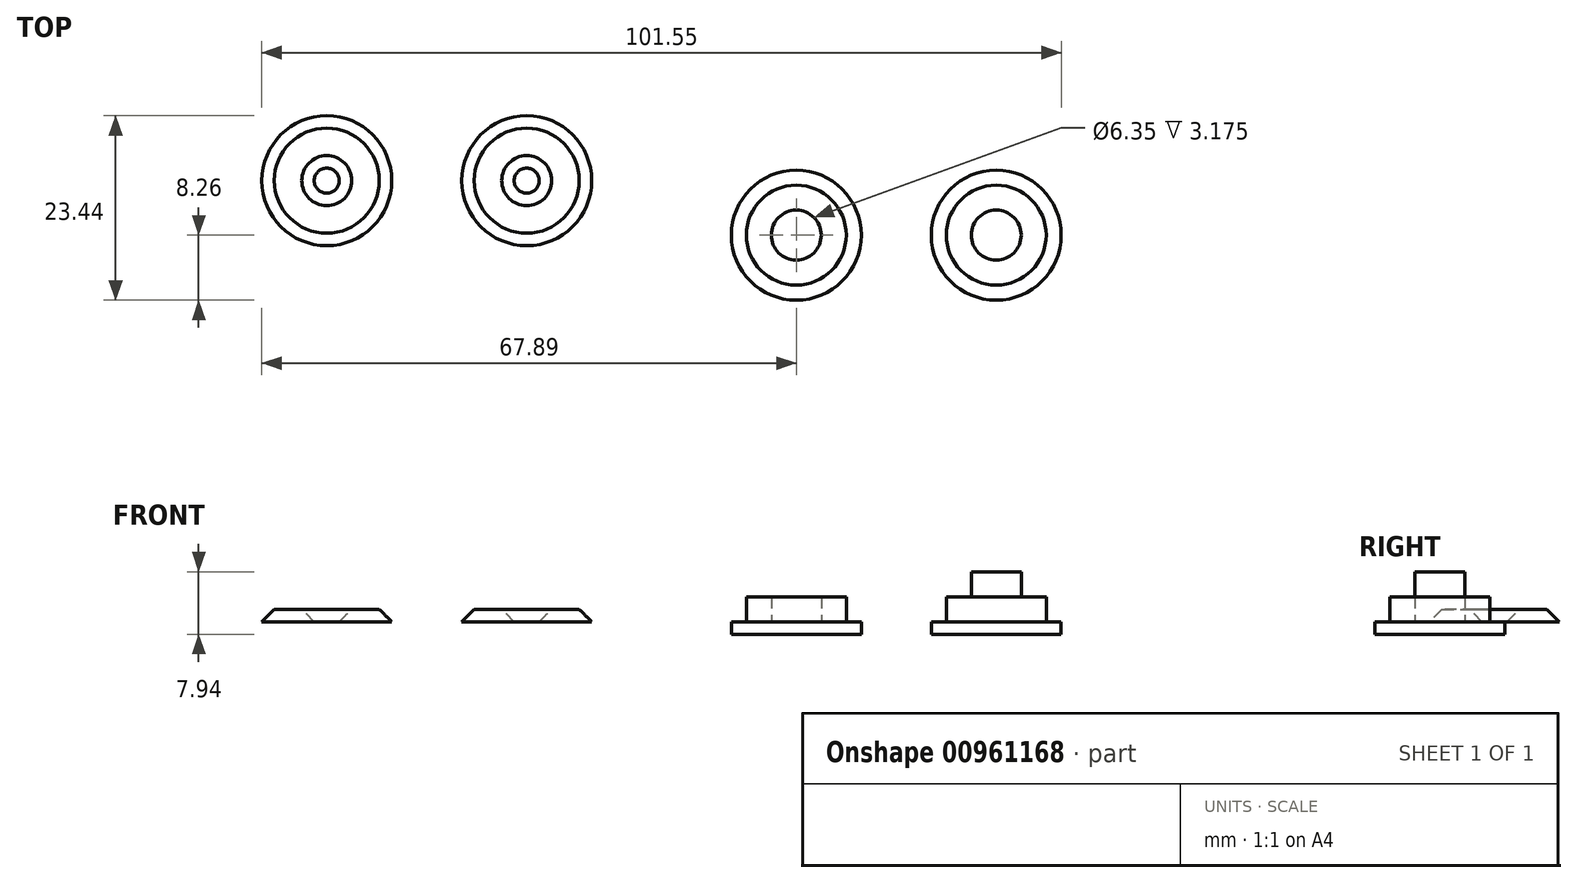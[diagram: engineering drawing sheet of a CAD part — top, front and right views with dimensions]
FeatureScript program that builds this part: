
annotation { "Feature Type Name" : "Feature", "Feature Type Description" : "" }
export const myFeature = defineFeature(function(context is Context, id is Id, definition is map)
    precondition{}
    {
        {
            var Q0;
            Q0=qCreatedBy(makeId("Top.planeOp"),FACE);
            var sketch = newSketch(context, id + "F0", { "sketchPlane" : qUnion([Q0])});
            skCircle(sketch, "E0", {"center": v(0, 0) * mm, "radius": 6.35 * mm});
            skCircle(sketch, "E1", {"center": v(0, 0) * mm, "radius": 3.18 * mm});
            skSolve(sketch);
        }
        {
            var Q0;
            Q0=qSketchRegion(id+"F0",true);
            extrude(context, id + "F1", {"entities" : qUnion([Q0]), "depth" : 3.17 * mm, "offsetDistance" : 25.4 * mm});
        }
        {
            var Q0;
            Q0=makeQuery(id+"F1.opExtrude","CAP_FACE",FACE,{"disambiguationData":[OSD([sQuery(id+"F0.wireOp",EDGE,"E0"),sQuery(id+"F0.wireOp",EDGE,"E1")])],"isStart":true});
            var sketch = newSketch(context, id + "F2", { "sketchPlane" : qUnion([Q0])});
            skCircle(sketch, "E2", {"center": v(0, 0) * mm, "radius": 8.26 * mm});
            skSolve(sketch);
        }
        {
            var Q0;
            Q0=qSketchRegion(id+"F2",true);
            extrude(context, id + "F3", {"entities" : qUnion([Q0]), "operationType" : NewBodyOperationType.ADD, "depth" : 3.17 * mm, "offsetDistance" : 25.4 * mm});
        }
        {
            var Q0;
            Q0=makeQuery(id+"F1.opExtrude","SWEPT_BODY",BODY,{"disambiguationData":[OSD([sQuery(id+"F0.wireOp",EDGE,"E0"),sQuery(id+"F0.wireOp",EDGE,"E1")])]});
            var Q1;
            Q1=qCreatedBy(makeId("Right.planeOp"),FACE);
            transform(context, id + "F4", {"entities" : qUnion([Q0]), "transformType" : TransformType.TRANSLATION_DISTANCE, "transformDirection" : qUnion([Q1]), "distance" : 25.4 * mm, "makeCopy" : true});
        }
        {
            var Q0;
            Q0=qCreatedBy(makeId("Top.planeOp"),FACE);
            var sketch = newSketch(context, id + "F5", { "sketchPlane" : qUnion([Q0])});
            skCircle(sketch, "E3", {"center": v(54.82, 6.15) * mm, "radius": 3.18 * mm});
            skSolve(sketch);
        }
        {
            var Q0;
            Q0=qSketchRegion(id+"F5",true);
            extrude(context, id + "F6", {"entities" : qUnion([Q0]), "depth" : 6.35 * mm, "offsetDistance" : 25.4 * mm});
        }
        {
            var Q0;
            Q0=makeQuery(id+"F6.opExtrude","CAP_FACE",FACE,{"disambiguationData":[OSD([sQuery(id+"F5.wireOp",EDGE,"E3")])],"isStart":false});
            var sketch = newSketch(context, id + "F7", { "sketchPlane" : qUnion([Q0])});
            skLineSegment(sketch, "E4.bottom", {"start": v(54.82, 4.88) * mm, "end": v(58.63, 4.88) * mm});
            skLineSegment(sketch, "E4.top", {"start": v(54.82, 7.42) * mm, "end": v(58.63, 7.42) * mm});
            skLineSegment(sketch, "E4.left", {"start": v(54.82, 4.88) * mm, "end": v(54.82, 7.42) * mm});
            skLineSegment(sketch, "E4.right", {"start": v(58.63, 4.88) * mm, "end": v(58.63, 7.42) * mm});
            skLineSegment(sketch, "E5", {"start": v(54.82, 6.15) * mm, "end": v(54.82, 2.98) * mm});
            skLineSegment(sketch, "E6", {"start": v(54.82, 2.98) * mm, "end": v(54.82, 9.33) * mm});
            skSolve(sketch);
        }
        {
            var Q0;
            Q0=qSketchRegion(id+"F7",true);
            extrude(context, id + "F8", {"entities" : qUnion([Q0]), "operationType" : NewBodyOperationType.ADD, "oppositeDirection" : true, "depth" : 3.17 * mm, "offsetDistance" : 25.4 * mm});
        }
        {
            var Q0;
            Q0=makeQuery(id+"F6.opExtrude","SWEPT_BODY",BODY,{"disambiguationData":[OSD([sQuery(id+"F5.wireOp",EDGE,"E3")])]});
            deleteBodies(context, id + "F9", {"entities" : qUnion([Q0])});
        }
        {
            var Q0;
            Q0=makeQuery(id+"F4.opPattern","COPY",FACE,{"derivedFrom":makeQuery(id+"F3.boolean.opBoolean","SPLIT",FACE,{"disambiguationData":[TD([makeQuery(id+"F1.opExtrude","SWEPT_FACE",FACE,{"disambiguationData":[OSD([sQuery(id+"F0.wireOp",EDGE,"E1")])]})])],"derivedFrom":makeQuery(id+"F3.opExtrude","CAP_FACE",FACE,{"disambiguationData":[OSD([sQuery(id+"F2.wireOp",EDGE,"E2")])],"isStart":true})}),"instanceName":"1"});
            extrude(context, id + "F10", {"entities" : qUnion([Q0]), "operationType" : NewBodyOperationType.ADD, "depth" : 6.35 * mm, "offsetDistance" : 25.4 * mm});
        }
        {
            var Q0;
            Q0=makeQuery(id+"F4.opPattern","COPY",FACE,{"derivedFrom":makeQuery(id+"F3.opExtrude","CAP_FACE",FACE,{"disambiguationData":[OSD([sQuery(id+"F2.wireOp",EDGE,"E2")])],"isStart":false}),"instanceName":"1"});
            extrude(context, id + "F11", {"entities" : qUnion([Q0]), "operationType" : NewBodyOperationType.REMOVE, "oppositeDirection" : true, "depth" : 1.59 * mm, "offsetDistance" : 25.4 * mm});
        }
        {
            var Q0;
            Q0=qCreatedBy(makeId("Top.planeOp"),FACE);
            var sketch = newSketch(context, id + "F12", { "sketchPlane" : qUnion([Q0])});
            skCircle(sketch, "E7", {"center": v(-34.24, 6.92) * mm, "radius": 8.26 * mm});
            skSolve(sketch);
        }
        {
            var Q0;
            Q0=qSketchRegion(id+"F12",true);
            extrude(context, id + "F13", {"entities" : qUnion([Q0]), "depth" : 1.59 * mm, "offsetDistance" : 25.4 * mm, "hasDraft" : true, "draftAngle" : 45 * degree, "draftPullDirection" : true});
        }
        {
            var Q0;
            Q0=makeQuery(id+"F13.opExtrude","CAP_FACE",FACE,{"disambiguationData":[OSD([sQuery(id+"F12.wireOp",EDGE,"E7")])],"isStart":false});
            var sketch = newSketch(context, id + "F14", { "sketchPlane" : qUnion([Q0])});
            skCircle(sketch, "E8", {"center": v(-34.24, 6.92) * mm, "radius": 3.17 * mm});
            skSolve(sketch);
        }
        {
            var Q0;
            Q0=makeQuery(id+"F14.imprint","IMPRINT",FACE,{"disambiguationData":[TD([[makeQuery(id+"F14.imprint","IMPRINT",EDGE,{"derivedFrom":sQuery(id+"F14.wireOp",EDGE,"E8")}),1.0]])]});
            extrude(context, id + "F15", {"entities" : qUnion([Q0]), "operationType" : NewBodyOperationType.REMOVE, "oppositeDirection" : true, "depth" : 25.4 * mm, "offsetDistance" : 25.4 * mm, "hasDraft" : true, "draftAngle" : 45 * degree, "draftPullDirection" : true});
        }
        {
            var Q0;
            Q0=makeQuery(id+"F3.opExtrude","CAP_FACE",FACE,{"disambiguationData":[OSD([sQuery(id+"F2.wireOp",EDGE,"E2")])],"isStart":false});
            extrude(context, id + "F16", {"entities" : qUnion([Q0]), "operationType" : NewBodyOperationType.REMOVE, "oppositeDirection" : true, "depth" : 1.59 * mm, "offsetDistance" : 25.4 * mm});
        }
        {
            var Q0;
            Q0=makeQuery(id+"F13.opExtrude","SWEPT_BODY",BODY,{"disambiguationData":[OSD([sQuery(id+"F12.wireOp",EDGE,"E7")])]});
            var Q1;
            Q1=qCreatedBy(makeId("Right.planeOp"),FACE);
            transform(context, id + "F17", {"entities" : qUnion([Q0]), "transformType" : TransformType.TRANSLATION_DISTANCE, "transformDirection" : qUnion([Q1]), "distance" : 25.4 * mm, "oppositeDirection" : true, "makeCopy" : true});
        }
    });
